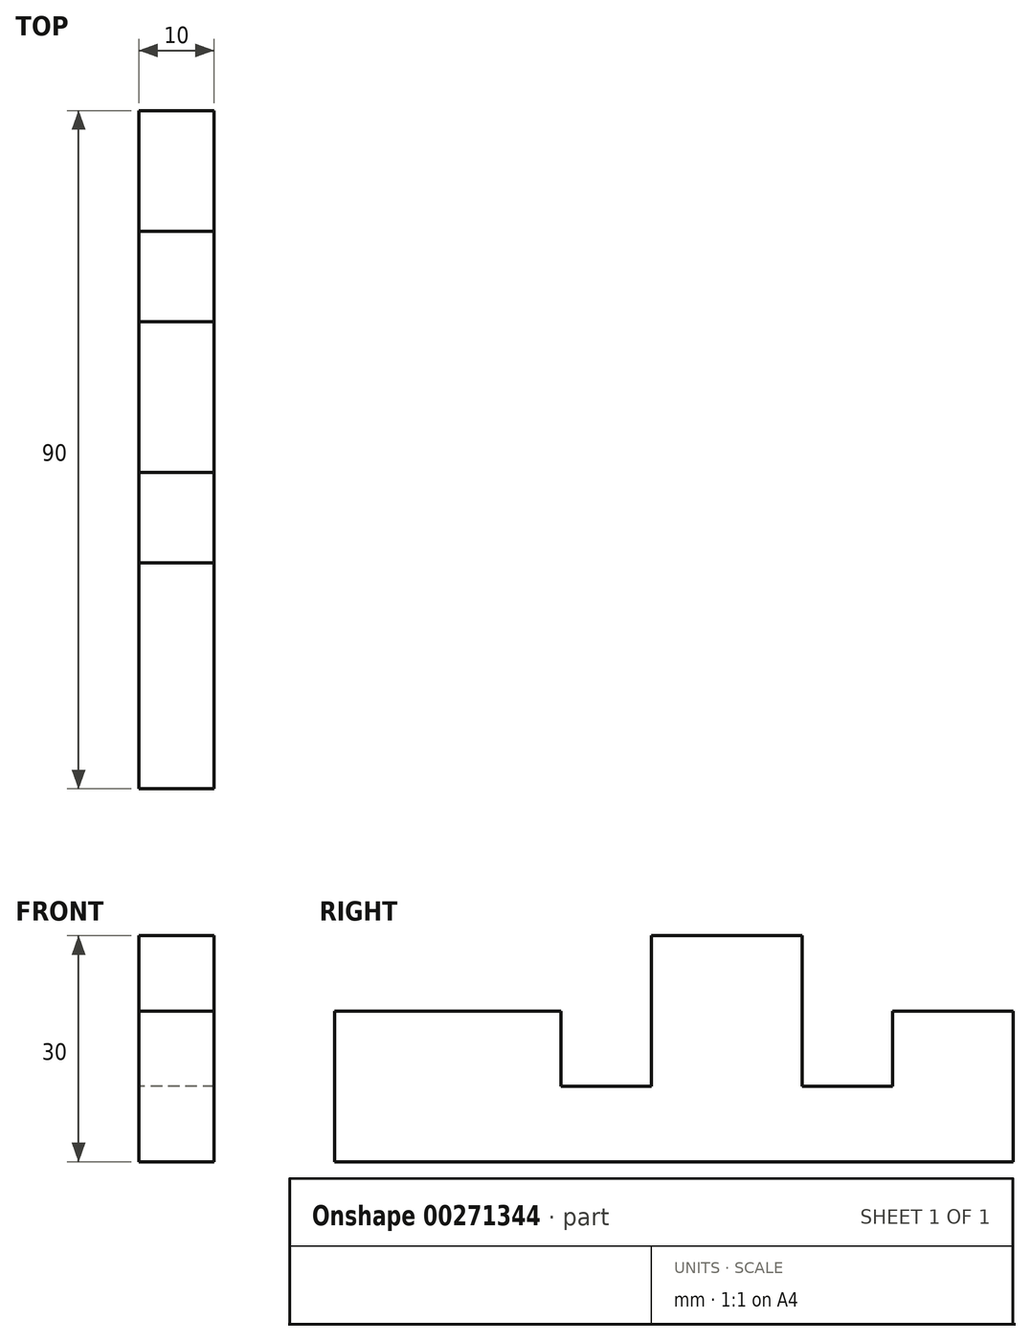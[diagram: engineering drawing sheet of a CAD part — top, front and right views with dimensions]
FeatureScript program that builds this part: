
annotation { "Feature Type Name" : "Feature", "Feature Type Description" : "" }
export const myFeature = defineFeature(function(context is Context, id is Id, definition is map)
    precondition{}
    {
        {
            var Q0;
            Q0=qCreatedBy(makeId("Right.planeOp"),FACE);
            var sketch = newSketch(context, id + "F0", { "sketchPlane" : qUnion([Q0])});
            skLineSegment(sketch, "E0", {"start": v(0, 0) * mm, "end": v(90, 0) * mm});
            skLineSegment(sketch, "E1", {"start": v(0, 0) * mm, "end": v(0, 20) * mm});
            skLineSegment(sketch, "E2", {"start": v(0, 20) * mm, "end": v(30, 20) * mm});
            skLineSegment(sketch, "E3", {"start": v(30, 20) * mm, "end": v(30, 10) * mm});
            skLineSegment(sketch, "E4", {"start": v(30, 10) * mm, "end": v(42, 10) * mm});
            skLineSegment(sketch, "E5", {"start": v(42, 10) * mm, "end": v(42, 30) * mm});
            skLineSegment(sketch, "E6", {"start": v(42, 30) * mm, "end": v(62, 30) * mm});
            skLineSegment(sketch, "E7", {"start": v(62, 30) * mm, "end": v(62, 10) * mm});
            skLineSegment(sketch, "E8", {"start": v(62, 10) * mm, "end": v(74, 10) * mm});
            skLineSegment(sketch, "E9", {"start": v(74, 10) * mm, "end": v(74, 20) * mm});
            skLineSegment(sketch, "E10", {"start": v(90, 0) * mm, "end": v(90, 20) * mm});
            skPoint(sketch, "E10.endSnap0", {"position": v(15, 20) * mm});
            skLineSegment(sketch, "E11", {"start": v(90, 20) * mm, "end": v(74, 20) * mm});
            skSolve(sketch);
        }
        {
            var Q0;
            Q0=makeQuery(id+"F0.imprint","IMPRINT",FACE,{"disambiguationData":[TD([[makeQuery(id+"F0.imprint","IMPRINT",EDGE,{"derivedFrom":sQuery(id+"F0.wireOp",EDGE,"E0")}),1.0]])]});
            extrude(context, id + "F1", {"entities" : qUnion([Q0]), "depth" : 10 * mm});
        }
    });
